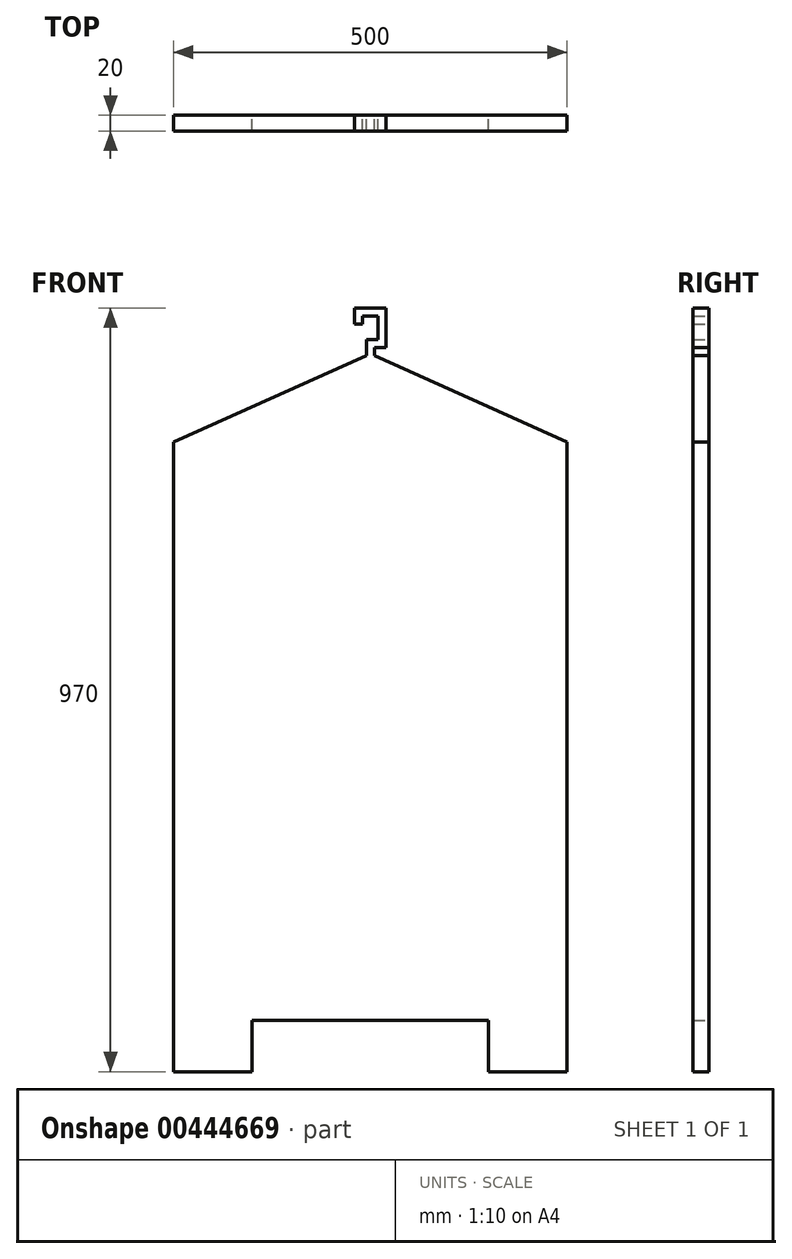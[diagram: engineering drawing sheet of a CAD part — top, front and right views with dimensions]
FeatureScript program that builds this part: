
annotation { "Feature Type Name" : "Feature", "Feature Type Description" : "" }
export const myFeature = defineFeature(function(context is Context, id is Id, definition is map)
    precondition{}
    {
        {
            var Q0;
            Q0=qCreatedBy(makeId("Front.planeOp"),FACE);
            var sketch = newSketch(context, id + "F0", { "sketchPlane" : qUnion([Q0])});
            skLineSegment(sketch, "E0.bottom", {"start": v(0, 0) * mm, "end": v(100, 0) * mm});
            skLineSegment(sketch, "E0.left", {"start": v(0, 0) * mm, "end": v(0, 800) * mm});
            skLineSegment(sketch, "E0.right", {"start": v(500, 0) * mm, "end": v(500, 800) * mm});
            skLineSegment(sketch, "E1.top", {"start": v(100, 65) * mm, "end": v(400, 65) * mm});
            skLineSegment(sketch, "E1.left", {"start": v(100, 0) * mm, "end": v(100, 65) * mm});
            skLineSegment(sketch, "E1.right", {"start": v(400, 0) * mm, "end": v(400, 65) * mm});
            skLineSegment(sketch, "E2.trimOffspring", {"start": v(400, 0) * mm, "end": v(500, 0) * mm});
            skLineSegment(sketch, "E3.bottom", {"start": v(230, 970) * mm, "end": v(270, 970) * mm});
            skLineSegment(sketch, "E3.top", {"start": v(240, 960) * mm, "end": v(260, 960) * mm});
            skLineSegment(sketch, "E3.left", {"start": v(230, 970) * mm, "end": v(230, 960) * mm});
            skLineSegment(sketch, "E3.right", {"start": v(270, 970) * mm, "end": v(270, 960) * mm});
            skLineSegment(sketch, "E4.top", {"start": v(230, 950) * mm, "end": v(240, 950) * mm});
            skLineSegment(sketch, "E4.left", {"start": v(230, 960) * mm, "end": v(230, 950) * mm});
            skLineSegment(sketch, "E4.right", {"start": v(240, 960) * mm, "end": v(240, 950) * mm});
            skLineSegment(sketch, "E5.left", {"start": v(270, 960) * mm, "end": v(270, 930) * mm});
            skLineSegment(sketch, "E5.right", {"start": v(260, 960) * mm, "end": v(260, 930) * mm});
            skLineSegment(sketch, "E6.bottom", {"start": v(260, 930) * mm, "end": v(245, 930) * mm});
            skLineSegment(sketch, "E6.top", {"start": v(270, 920) * mm, "end": v(255, 920) * mm});
            skLineSegment(sketch, "E6.left", {"start": v(270, 930) * mm, "end": v(270, 920) * mm});
            skLineSegment(sketch, "E6.right", {"start": v(245, 930) * mm, "end": v(245, 920) * mm});
            skLineSegment(sketch, "E7.left", {"start": v(245, 920) * mm, "end": v(245, 910) * mm});
            skLineSegment(sketch, "E7.right", {"start": v(255, 920) * mm, "end": v(255, 910) * mm});
            skLineSegment(sketch, "E8", {"start": v(0, 800) * mm, "end": v(245, 910) * mm});
            skLineSegment(sketch, "E9", {"start": v(255, 910) * mm, "end": v(500, 800) * mm});
            skPoint(sketch, "E10.left.start.orphan", {"position": v(250, 910) * mm});
            skSolve(sketch);
        }
        {
            var Q0;
            Q0 = qSketchRegion(id + "F0", true);
            extrude(context, id + "F1", {"entities" : qUnion([Q0]), "depth" : 20 * mm});
        }
    });
